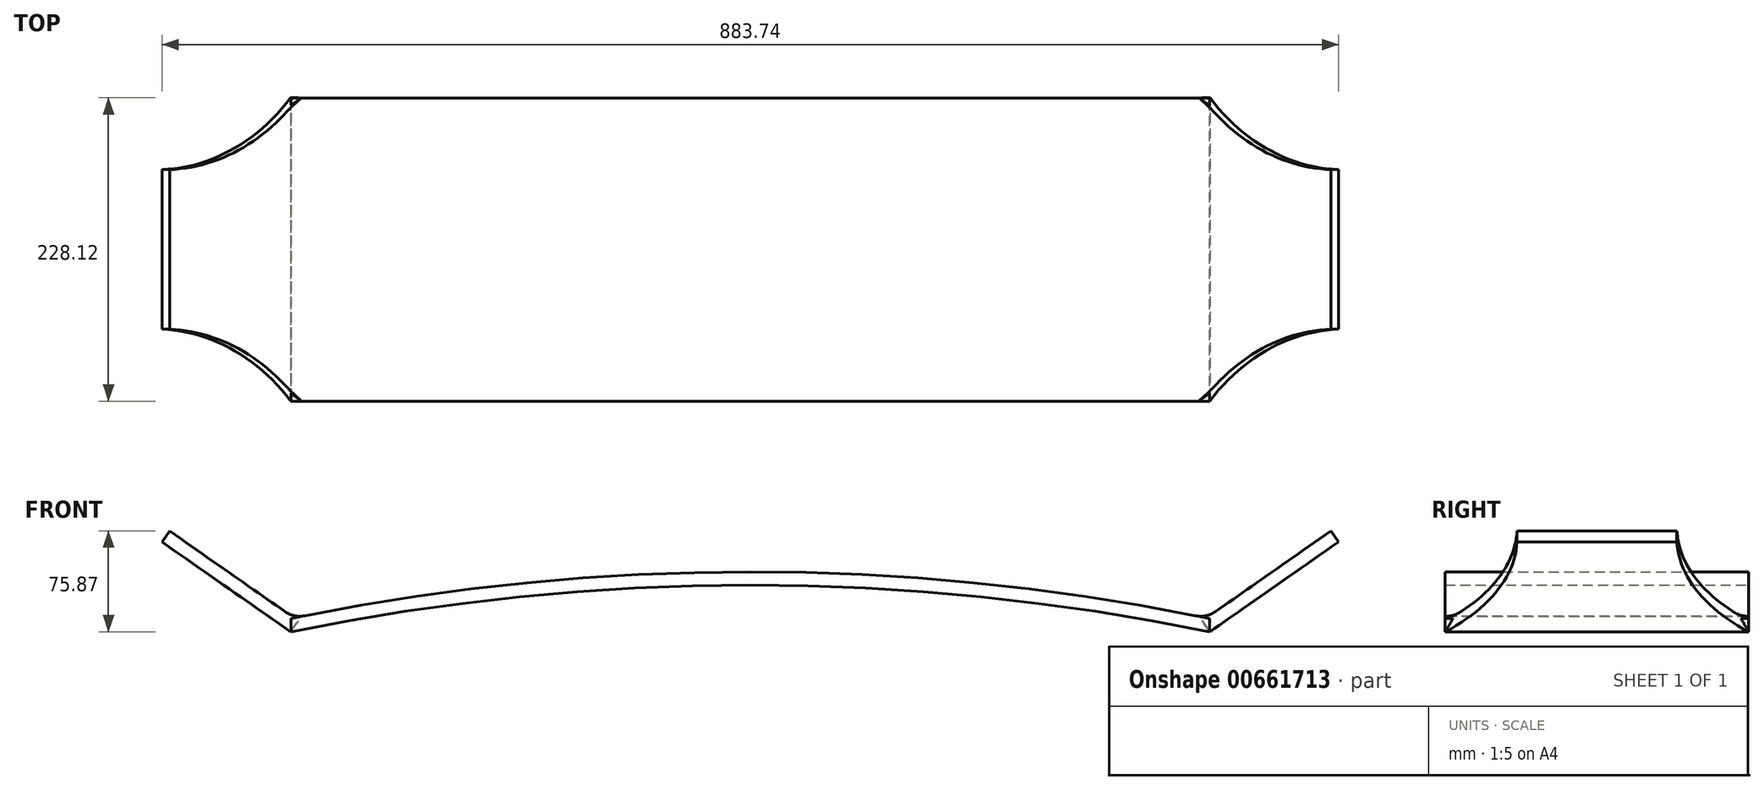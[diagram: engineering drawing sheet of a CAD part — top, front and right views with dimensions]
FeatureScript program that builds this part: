
annotation { "Feature Type Name" : "Feature", "Feature Type Description" : "" }
export const myFeature = defineFeature(function(context is Context, id is Id, definition is map)
    precondition{}
    {
        {
            var Q0;
            Q0=qCreatedBy(makeId("Front.planeOp"),FACE);
            var sketch = newSketch(context, id + "F0", { "sketchPlane" : qUnion([Q0])});
            skArc(sketch, "E0", {"start": v(357.86, 0) * mm, "mid": v(12.86, 35.05) * mm, "end": v(-332.14, 0) * mm});
            skLineSegment(sketch, "E1", {"start": v(-332.14, 0) * mm, "end": v(-332.14, 10) * mm});
            skLineSegment(sketch, "E2", {"start": v(357.86, 0) * mm, "end": v(357.86, 10) * mm});
            skArc(sketch, "E3", {"start": v(357.86, 10) * mm, "mid": v(12.86, 45.05) * mm, "end": v(-332.14, 10) * mm});
            skSolve(sketch);
        }
        {
            var Q0;
            Q0 = qSketchRegion(id + "F0", true);
            extrude(context, id + "F1", {"entities" : qUnion([Q0]), "endBound" : BoundingType.SYMMETRIC, "depth" : 228 * mm, "offsetDistance" : 25 * mm});
        }
        {
            var Q0;
            Q0=qCreatedBy(makeId("Top.planeOp"),FACE);
            var sketch = newSketch(context, id + "F2", { "sketchPlane" : qUnion([Q0])});
            skLineSegment(sketch, "E4", {"start": v(5.1, 112.22) * mm, "end": v(5.1, -115.78) * mm});
            skLineSegment(sketch, "E5", {"start": v(123.1, 58.22) * mm, "end": v(123.1, -61.78) * mm});
            skArc(sketch, "E6", {"start": v(123.1, -61.78) * mm, "mid": v(58.68, -76.93) * mm, "end": v(5.1, -115.78) * mm});
            skArc(sketch, "E7.MirrorCS", {"start": v(123.1, 58.22) * mm, "mid": v(58.68, 73.36) * mm, "end": v(5.1, 112.22) * mm});
            skSolve(sketch);
        }
        {
            var Q0;
            Q0 = qSketchRegion(id + "F2", true);
            extrude(context, id + "F3", {"entities" : qUnion([Q0]), "depth" : 10 * mm, "offsetDistance" : 25 * mm});
        }
        {
            var Q0;
            Q0=makeQuery(id+"F3.opExtrude","SWEPT_BODY",BODY,{"disambiguationData":[OSD([sQuery(id+"F2.wireOp",EDGE,"E4"),sQuery(id+"F2.wireOp",EDGE,"E5"),sQuery(id+"F2.wireOp",EDGE,"E6"),sQuery(id+"F2.wireOp",EDGE,"E7.MirrorCS")])]});
            var Q1;
            Q1=sQuery(id+"F2.wireOp",EDGE,"E4");
            transform(context, id + "F4", {"entities" : qUnion([Q0]), "transformType" : TransformType.ROTATION, "transformAxis" : qUnion([Q1]), "angle" : 35 * degree, "makeCopy" : false});
        }
        {
            var Q0;
            Q0=makeQuery(id+"F3.opExtrude","SWEPT_BODY",BODY,{"disambiguationData":[OSD([sQuery(id+"F2.wireOp",EDGE,"E4"),sQuery(id+"F2.wireOp",EDGE,"E5"),sQuery(id+"F2.wireOp",EDGE,"E6"),sQuery(id+"F2.wireOp",EDGE,"E7.MirrorCS")])]});
            transform(context, id + "F5", {"entities" : qUnion([Q0]), "transformType" : TransformType.TRANSLATION_3D, "dx" : 352.9 * mm, "dy" : 1.9 * mm, "dz" : 0 * mm, "makeCopy" : false});
        }
        {
            var Q0;
            Q0=makeQuery(id+"F3.opExtrude","SWEPT_BODY",BODY,{"disambiguationData":[OSD([sQuery(id+"F2.wireOp",EDGE,"E4"),sQuery(id+"F2.wireOp",EDGE,"E5"),sQuery(id+"F2.wireOp",EDGE,"E6"),sQuery(id+"F2.wireOp",EDGE,"E7.MirrorCS")])]});
            var Q1;
            Q1=qCreatedBy(makeId("Right.planeOp"),FACE);
            mirror(context, id + "F6", {"entities" : qUnion([Q0]), "mirrorPlane" : qUnion([Q1])});
        }
        {
            var Q0;
            Q0=makeQuery(id+"F6.opPattern","COPY",BODY,{"derivedFrom":makeQuery(id+"F3.opExtrude","SWEPT_BODY",BODY,{"disambiguationData":[OSD([sQuery(id+"F2.wireOp",EDGE,"E4"),sQuery(id+"F2.wireOp",EDGE,"E5"),sQuery(id+"F2.wireOp",EDGE,"E6"),sQuery(id+"F2.wireOp",EDGE,"E7.MirrorCS")])]}),"instanceName":"1"});
            transform(context, id + "F7", {"entities" : qUnion([Q0]), "transformType" : TransformType.TRANSLATION_3D, "dx" : 25.6 * mm, "dy" : 0 * mm, "dz" : 0 * mm, "makeCopy" : false});
        }
        {
            var Q0;
            Q0=makeQuery(id+"F6.opPattern","COPY",BODY,{"derivedFrom":makeQuery(id+"F3.opExtrude","SWEPT_BODY",BODY,{"disambiguationData":[OSD([sQuery(id+"F2.wireOp",EDGE,"E4"),sQuery(id+"F2.wireOp",EDGE,"E5"),sQuery(id+"F2.wireOp",EDGE,"E6"),sQuery(id+"F2.wireOp",EDGE,"E7.MirrorCS")])]}),"instanceName":"1"});
            var Q1;
            Q1=makeQuery(id+"F1.opExtrude","SWEPT_BODY",BODY,{"disambiguationData":[OSD([sQuery(id+"F0.wireOp",EDGE,"E0"),sQuery(id+"F0.wireOp",EDGE,"E1"),sQuery(id+"F0.wireOp",EDGE,"E2"),sQuery(id+"F0.wireOp",EDGE,"E3")])]});
            var Q2;
            Q2=makeQuery(id+"F3.opExtrude","SWEPT_BODY",BODY,{"disambiguationData":[OSD([sQuery(id+"F2.wireOp",EDGE,"E4"),sQuery(id+"F2.wireOp",EDGE,"E5"),sQuery(id+"F2.wireOp",EDGE,"E6"),sQuery(id+"F2.wireOp",EDGE,"E7.MirrorCS")])]});
            booleanBodies(context, id + "F8", {"operationType" : BooleanOperationType.UNION, "tools" : qUnion([Q0, Q1, Q2])});
        }
        {
            var Q0;
            Q0=makeQuery(id+"F8.opBoolean","INTERSECT",EDGE,{"derivedFrom":[makeQuery(id+"F1.opExtrude","SWEPT_FACE",FACE,{"disambiguationData":[OSD([sQuery(id+"F0.wireOp",EDGE,"E3")])]}),makeQuery(id+"F6.opPattern","COPY",FACE,{"derivedFrom":makeQuery(id+"F3.opExtrude","CAP_FACE",FACE,{"disambiguationData":[OSD([sQuery(id+"F2.wireOp",EDGE,"E4"),sQuery(id+"F2.wireOp",EDGE,"E5"),sQuery(id+"F2.wireOp",EDGE,"E6"),sQuery(id+"F2.wireOp",EDGE,"E7.MirrorCS")])],"isStart":false}),"instanceName":"1"})]});
            fillet(context, id + "F9", {"entities" : qUnion([Q0]), "radius" : 20 * mm, "tangentPropagation" : true, "rho" : 0.5, "crossSection" : FilletCrossSection.CONIC, "allowEdgeOverflow" : false});
        }
        {
            var Q0;
            Q0=makeQuery(id+"F8.opBoolean","INTERSECT",EDGE,{"derivedFrom":[makeQuery(id+"F1.opExtrude","SWEPT_FACE",FACE,{"disambiguationData":[OSD([sQuery(id+"F0.wireOp",EDGE,"E3")])]}),makeQuery(id+"F3.opExtrude","CAP_FACE",FACE,{"disambiguationData":[OSD([sQuery(id+"F2.wireOp",EDGE,"E4"),sQuery(id+"F2.wireOp",EDGE,"E5"),sQuery(id+"F2.wireOp",EDGE,"E6"),sQuery(id+"F2.wireOp",EDGE,"E7.MirrorCS")])],"isStart":false})]});
            fillet(context, id + "F10", {"entities" : qUnion([Q0]), "radius" : 20 * mm, "tangentPropagation" : true, "rho" : 0.5, "crossSection" : FilletCrossSection.CONIC, "allowEdgeOverflow" : false});
        }
    });
